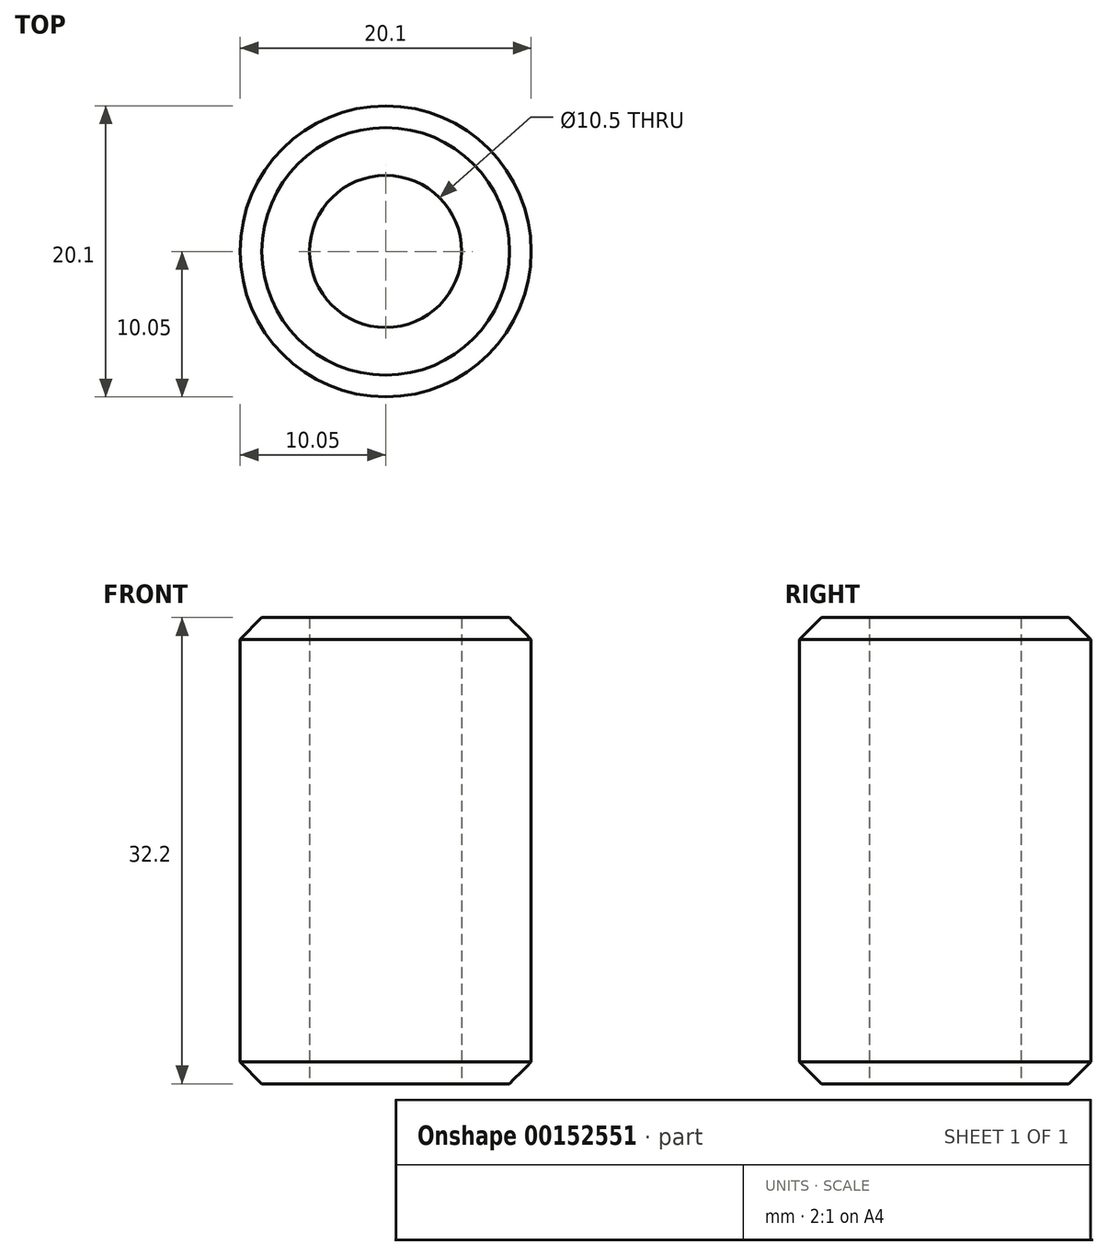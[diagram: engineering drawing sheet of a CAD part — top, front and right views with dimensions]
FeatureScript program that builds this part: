
annotation { "Feature Type Name" : "Feature", "Feature Type Description" : "" }
export const myFeature = defineFeature(function(context is Context, id is Id, definition is map)
    precondition{}
    {
        {
            var Q0;
            Q0=qCreatedBy(makeId("Top.planeOp"),FACE);
            var sketch = newSketch(context, id + "F0", { "sketchPlane" : qUnion([Q0])});
            skCircle(sketch, "E0", {"center": v(0, 0) * mm, "radius": 10.05 * mm});
            skCircle(sketch, "E1", {"center": v(0, 0) * mm, "radius": 5.25 * mm});
            skSolve(sketch);
        }
        {
            var Q0;
            Q0 = qSketchRegion(id + "F0", true);
            extrude(context, id + "F1", {"entities" : qUnion([Q0]), "depth" : 32.2 * mm});
        }
        {
            var Q0;
            Q0=makeQuery(id+"F1.opExtrude","SWEPT_FACE",FACE,{"disambiguationData":[OSD([sQuery(id+"F0.wireOp",EDGE,"E0")])]});
            chamfer(context, id + "F2", {"entities" : qUnion([Q0]), "width" : 1.5 * mm, "tangentPropagation" : true});
        }
    });
